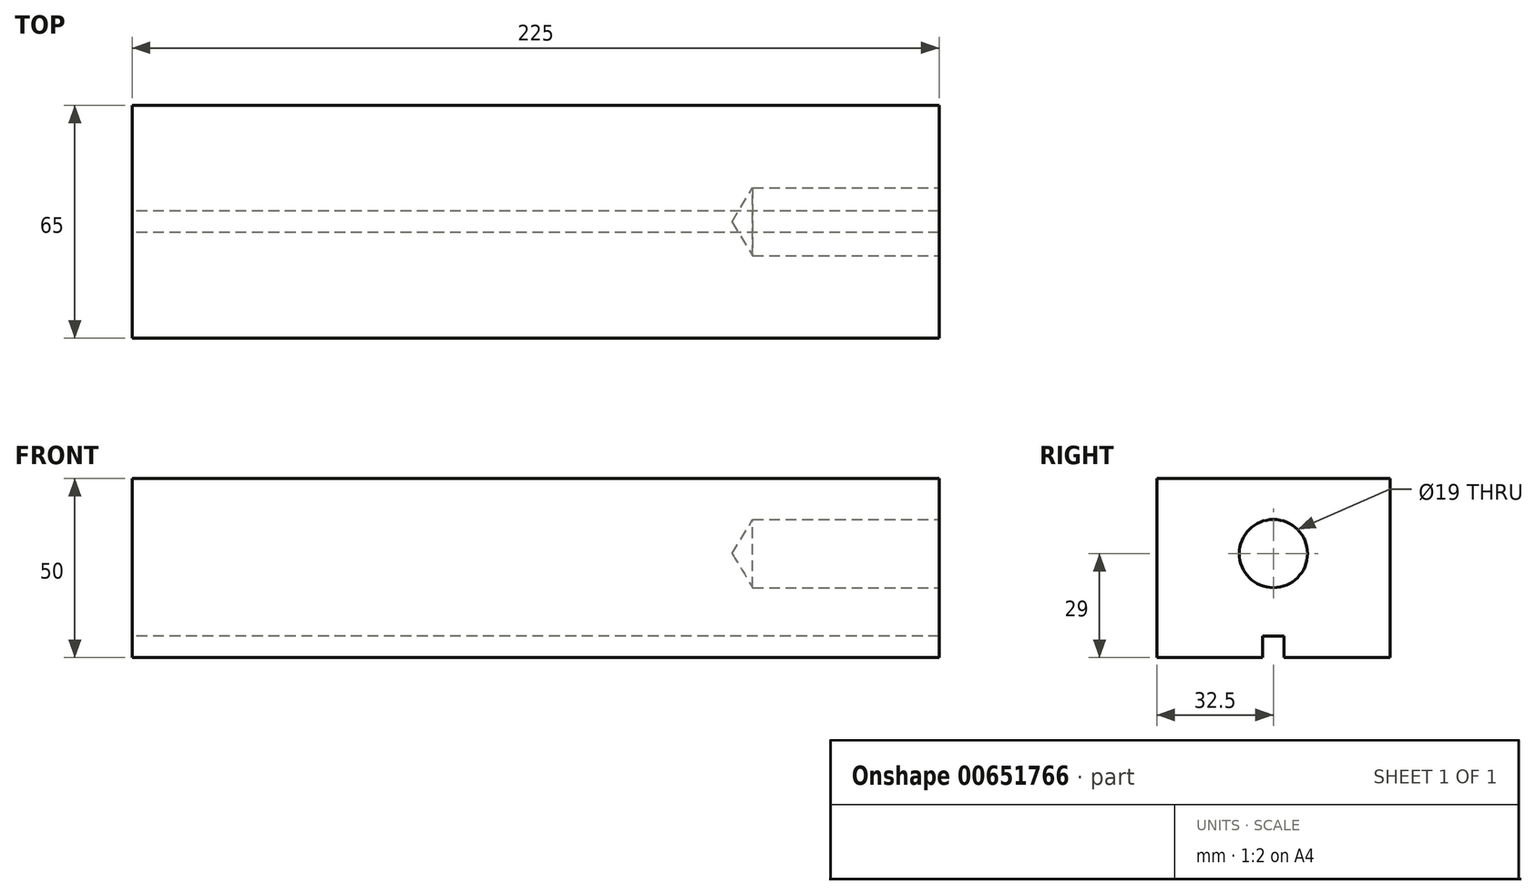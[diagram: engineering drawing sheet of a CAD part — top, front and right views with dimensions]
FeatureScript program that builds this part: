
annotation { "Feature Type Name" : "Feature", "Feature Type Description" : "" }
export const myFeature = defineFeature(function(context is Context, id is Id, definition is map)
    precondition{}
    {
        {
            var Q0;
            Q0=qCreatedBy(makeId("Right.planeOp"),FACE);
            var sketch = newSketch(context, id + "F0", { "sketchPlane" : qUnion([Q0])});
            skLineSegment(sketch, "E0.bottom", {"start": v(3, 0) * mm, "end": v(32.5, 0) * mm});
            skLineSegment(sketch, "E0.top", {"start": v(0, 50) * mm, "end": v(32.5, 50) * mm});
            skLineSegment(sketch, "E0.left", {"start": v(0, 6) * mm, "end": v(0, 50) * mm});
            skLineSegment(sketch, "E0.right", {"start": v(32.5, 0) * mm, "end": v(32.5, 50) * mm});
            skLineSegment(sketch, "E1.top", {"start": v(0, 6) * mm, "end": v(3, 6) * mm});
            skLineSegment(sketch, "E1.right", {"start": v(3, 0) * mm, "end": v(3, 6) * mm});
            skSolve(sketch);
        }
        {
            var Q0;
            Q0 = qSketchRegion(id + "F0", true);
            extrude(context, id + "F1", {"entities" : qUnion([Q0]), "depth" : 225 * mm, "offsetDistance" : 25 * mm});
        }
        {
            var Q0;
            Q0=makeQuery(id+"F1.opExtrude","CAP_FACE",FACE,{"disambiguationData":[OSD([sQuery(id+"F0.wireOp",EDGE,"E0.bottom"),sQuery(id+"F0.wireOp",EDGE,"E0.top"),sQuery(id+"F0.wireOp",EDGE,"E0.left"),sQuery(id+"F0.wireOp",EDGE,"E0.right"),sQuery(id+"F0.wireOp",EDGE,"E1.top"),sQuery(id+"F0.wireOp",EDGE,"E1.right")])],"isStart":false});
            var sketch = newSketch(context, id + "F2", { "sketchPlane" : qUnion([Q0])});
            skLineSegment(sketch, "E2", {"start": v(32.5, 0) * mm, "end": v(32.5, 29) * mm, "construction": true});
            skLineSegment(sketch, "E3", {"start": v(32.5, 29) * mm, "end": v(0, 29) * mm, "construction": true});
            skPoint(sketch, "E3.endSnap0", {"position": v(0, 28) * mm});
            skPoint(sketch, "E4", {"position": v(0, 29) * mm});
            skSolve(sketch);
        }
        {
            var Q0;
            Q0=sQuery(id+"F2.wireOp",VERTEX,"E4");
            var Q1;
            Q1=makeQuery(id+"F1.opExtrude","SWEPT_BODY",BODY,{"disambiguationData":[OSD([sQuery(id+"F0.wireOp",EDGE,"E0.bottom"),sQuery(id+"F0.wireOp",EDGE,"E0.top"),sQuery(id+"F0.wireOp",EDGE,"E0.left"),sQuery(id+"F0.wireOp",EDGE,"E0.right"),sQuery(id+"F0.wireOp",EDGE,"E1.top"),sQuery(id+"F0.wireOp",EDGE,"E1.right")])]});
            hole(context, id + "F3", {"style" : HoleStyle.SIMPLE, "endStyle" : HoleEndStyle.BLIND, "holeDiameter" : 19 * mm, "majorDiameter" : 5 * mm, "holeDepth" : 52 * mm, "isTappedThrough" : true, "tappedDepth" : 12 * mm, "tapClearance" : 3, "locations" : qUnion([Q0]), "scope" : qUnion([Q1])});
        }
        {
            var Q0;
            Q0=makeQuery(id+"F1.opExtrude","SWEPT_BODY",BODY,{"disambiguationData":[OSD([sQuery(id+"F0.wireOp",EDGE,"E0.bottom"),sQuery(id+"F0.wireOp",EDGE,"E0.top"),sQuery(id+"F0.wireOp",EDGE,"E0.left"),sQuery(id+"F0.wireOp",EDGE,"E0.right"),sQuery(id+"F0.wireOp",EDGE,"E1.top"),sQuery(id+"F0.wireOp",EDGE,"E1.right")])]});
            var Q1;
            Q1=makeQuery(id+"F1.opExtrude","SWEPT_FACE",FACE,{"disambiguationData":[OSD([sQuery(id+"F0.wireOp",EDGE,"E0.left")])]});
            mirror(context, id + "F4", {"operationType" : NewBodyOperationType.ADD, "entities" : qUnion([Q0]), "mirrorPlane" : qUnion([Q1])});
        }
    });
